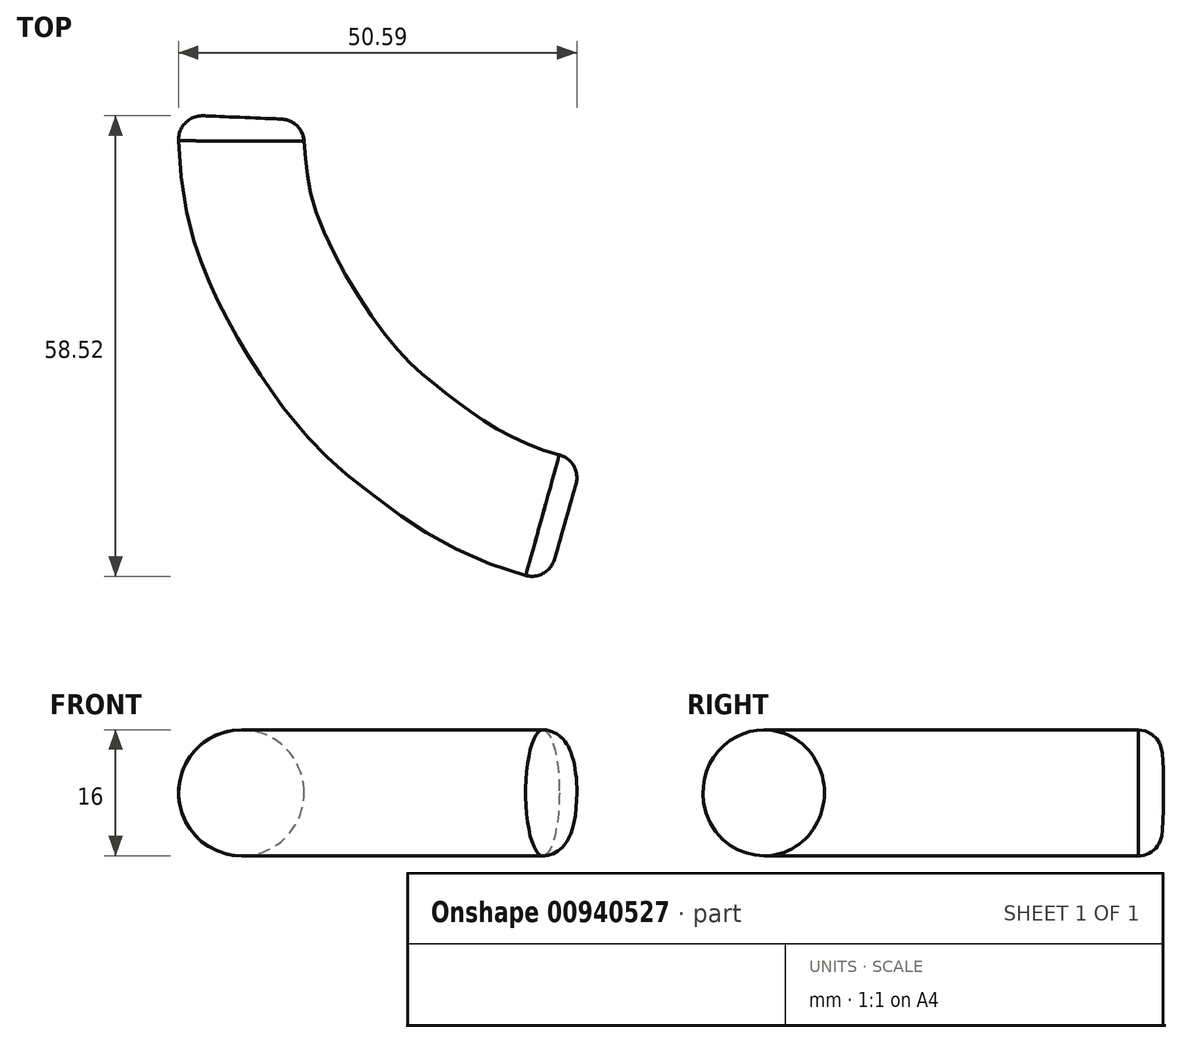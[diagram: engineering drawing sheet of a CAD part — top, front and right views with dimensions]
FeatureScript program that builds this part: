
annotation { "Feature Type Name" : "Feature", "Feature Type Description" : "" }
export const myFeature = defineFeature(function(context is Context, id is Id, definition is map)
    precondition{}
    {
        {
            var Q0;
            Q0=qCreatedBy(makeId("Top.planeOp"),FACE);
            var sketch = newSketch(context, id + "F0", { "sketchPlane" : qUnion([Q0])});
            skFitSpline(sketch, "E0", {"points": [v(-44.85, -0.03) * mm, v(-43.14, -11.62) * mm, v(-33.56, -28.27) * mm, v(-26.52, -34.82) * mm, v(-19.19, -39.81) * mm, v(-9.21, -43.2) * mm], "startDerivative": vector(5.33, -63.98) * mm, "endDerivative": vector(58.64, -9.09) * mm});
            skLineSegment(sketch, "E1", {"start": v(-9.21, -43.2) * mm, "end": v(-13.63, -58.57) * mm});
            skLineSegment(sketch, "E2", {"start": v(-13.63, -58.57) * mm, "end": v(-18.22, -46.32) * mm});
            skLineSegment(sketch, "E3", {"start": v(-18.22, -46.32) * mm, "end": v(-9.21, -43.2) * mm});
            skSolve(sketch);
        }
        {
            var Q0;
            Q0 = qSketchRegion(id + "F0", true);
            extrude(context, id + "F1", {"entities" : qUnion([Q0]), "endBound" : BoundingType.SYMMETRIC, "depth" : 16 * mm, "offsetDistance" : 25 * mm});
        }
        {
            var Q0;
            Q0=makeQuery(id+"F1.opExtrude","SWEPT_FACE",FACE,{"disambiguationData":[OSD([sQuery(id+"F0.wireOp",EDGE,"E1")])]});
            var sketch = newSketch(context, id + "F2", { "sketchPlane" : qUnion([Q0])});
            skCircle(sketch, "E4", {"center": v(-52.06, 0) * mm, "radius": 8 * mm});
            skPoint(sketch, "E4.centerSnap0", {"position": v(-52.06, 8) * mm});
            skPoint(sketch, "E4.centerSnap1", {"position": v(-60.06, 0) * mm});
            skSolve(sketch);
        }
        {
            var Q0;
            {var subQ1=sQuery(id+"F0.wireOp",EDGE,"E1");var subQ6=makeQuery(id+"F1.opExtrude","SWEPT_EDGE",EDGE,{"disambiguationData":[OSD([subQ1,sQuery(id+"F0.wireOp",EDGE,"E2")])]});Q0=makeQuery(id+"F2.imprint","IMPRINT",FACE,{"disambiguationData":[TD([[makeQuery(id+"F2.imprint","IMPRINT",EDGE,{"derivedFrom":subQ6}),1.0]])]});}
            var Q1;
            {var subQ1=sQuery(id+"F0.wireOp",EDGE,"E1");var subQ6=makeQuery(id+"F1.opExtrude","SWEPT_EDGE",EDGE,{"disambiguationData":[OSD([subQ1,sQuery(id+"F0.wireOp",EDGE,"E3")])]});Q1=makeQuery(id+"F2.imprint","IMPRINT",FACE,{"disambiguationData":[TD([[makeQuery(id+"F2.imprint","IMPRINT",EDGE,{"derivedFrom":subQ6}),-1.0]])]});}
            extrude(context, id + "F3", {"entities" : qUnion([Q0, Q1]), "operationType" : NewBodyOperationType.REMOVE, "oppositeDirection" : true, "depth" : 25 * mm, "offsetDistance" : 25 * mm});
        }
        {
            var Q0;
            Q0=makeQuery(id+"F1.opExtrude","SWEPT_FACE",FACE,{"disambiguationData":[OSD([sQuery(id+"F0.wireOp",EDGE,"E1")])]});
            var Q1;
            Q1=sQuery(id+"F0.wireOp",EDGE,"E0");
            sweep(context, id + "F4", {"profiles" : qUnion([Q0]), "path" : qUnion([Q1])});
        }
        {
            var Q0;
            Q0=makeQuery(id+"F1.opExtrude","SWEPT_BODY",BODY,{"disambiguationData":[OSD([sQuery(id+"F0.wireOp",EDGE,"E1"),sQuery(id+"F0.wireOp",EDGE,"E2"),sQuery(id+"F0.wireOp",EDGE,"E3")])]});
            deleteBodies(context, id + "F5", {"entities" : qUnion([Q0])});
        }
        {
            var Q0;
            Q0=makeQuery(id+"F4.opSweep","CAP_EDGE",EDGE,{"disambiguationData":[OSD([sQuery(id+"F0.wireOp",VERTEX,"E0.end"),sQuery(id+"F2.wireOp",EDGE,"E4")])],"isStart":true});
            var Q1;
            Q1=makeQuery(id+"F4.opSweep","CAP_EDGE",EDGE,{"disambiguationData":[OSD([sQuery(id+"F0.wireOp",VERTEX,"E0.start"),sQuery(id+"F2.wireOp",EDGE,"E4")])],"isStart":false});
            fillet(context, id + "F6", {"entities" : qUnion([Q0, Q1]), "radius" : 3 * mm, "tangentPropagation" : true, "allowEdgeOverflow" : false});
        }
    });
